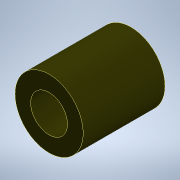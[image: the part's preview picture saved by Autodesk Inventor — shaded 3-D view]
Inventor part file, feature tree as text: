
AUTODESK INVENTOR PART (.ipt)
format: ipt  version: 2021 (Build 250183000, 183)  size: 105,472 bytes
history: native  units: mm
features: extrude x1, sketch x1
ambient origin geometry x8: Origin, YZ Plane, XZ Plane, XY Plane, X Axis, Y Axis, Z Axis, Center Point
bodies: Solid1 (feature_tree)
feature tree (2):
  extrude  "Extrusion1"  Depth=6.0mm
  sketch  "Sketch1"  dims[d0=5.0mm d1=2.7mm d2=6.0mm d3=0.0mm]
